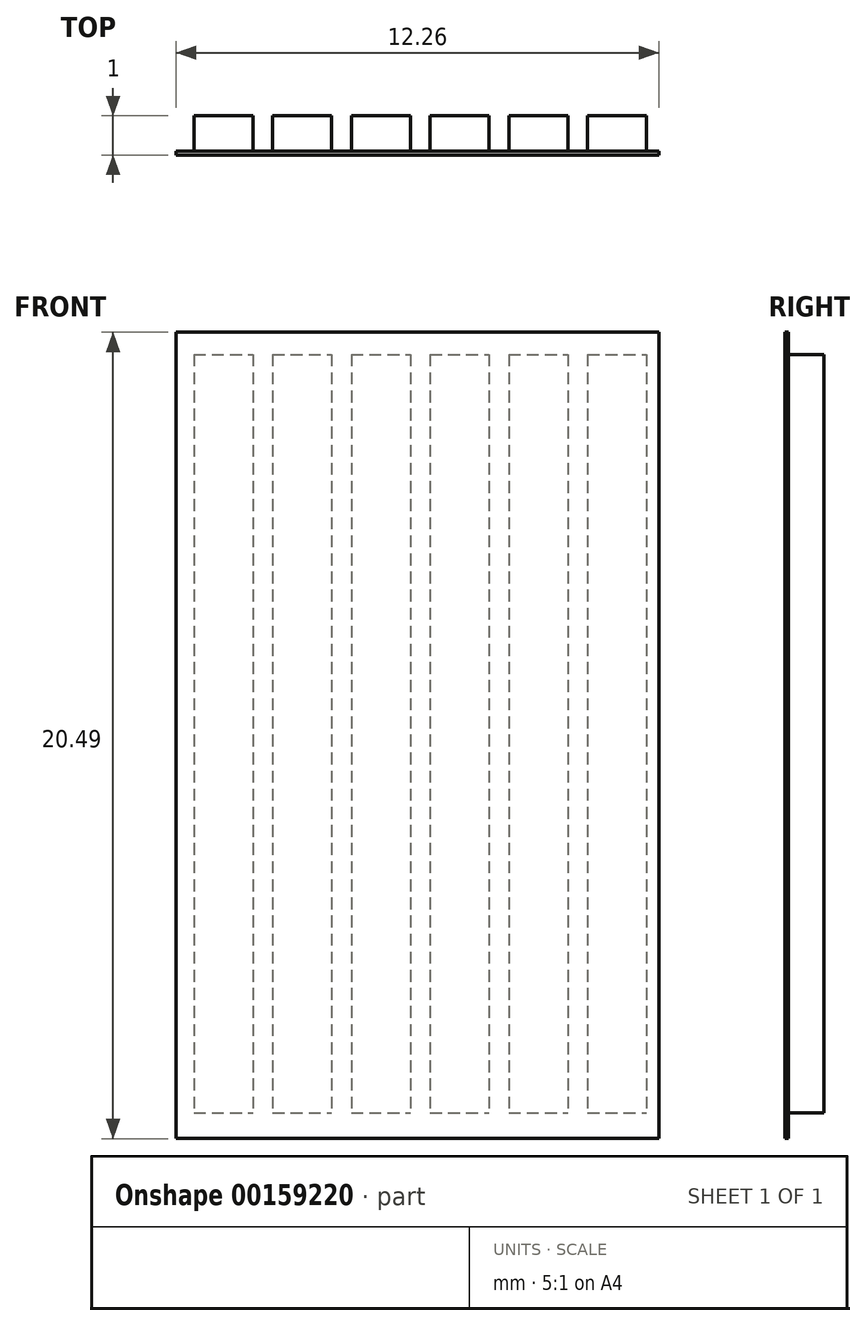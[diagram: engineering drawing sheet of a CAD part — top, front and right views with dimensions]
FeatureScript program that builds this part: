
annotation { "Feature Type Name" : "Feature", "Feature Type Description" : "" }
export const myFeature = defineFeature(function(context is Context, id is Id, definition is map)
    precondition{}
    {
        {
            var Q0;
            Q0=qCreatedBy(makeId("Front.planeOp"),FACE);
            var sketch = newSketch(context, id + "F0", { "sketchPlane" : qUnion([Q0])});
            skLineSegment(sketch, "E0.bottom", {"start": v(-57.17, 11.8) * mm, "end": v(-58.67, 11.8) * mm});
            skLineSegment(sketch, "E0.top", {"start": v(-57.17, 31.07) * mm, "end": v(-58.67, 31.07) * mm});
            skLineSegment(sketch, "E0.left", {"start": v(-57.17, 11.8) * mm, "end": v(-57.17, 31.07) * mm});
            skLineSegment(sketch, "E0.right", {"start": v(-58.67, 11.8) * mm, "end": v(-58.67, 31.07) * mm});
            skLineSegment(sketch, "E1.1.0.0", {"start": v(-56.67, 11.8) * mm, "end": v(-56.67, 31.07) * mm});
            skLineSegment(sketch, "E1.1.0.1", {"start": v(-55.17, 11.8) * mm, "end": v(-55.17, 31.07) * mm});
            skLineSegment(sketch, "E1.1.0.2", {"start": v(-55.17, 31.07) * mm, "end": v(-56.67, 31.07) * mm});
            skLineSegment(sketch, "E1.1.0.3", {"start": v(-55.17, 11.8) * mm, "end": v(-56.67, 11.8) * mm});
            skLineSegment(sketch, "E1.2.0.0", {"start": v(-54.67, 11.8) * mm, "end": v(-54.67, 31.07) * mm});
            skLineSegment(sketch, "E1.2.0.1", {"start": v(-53.17, 11.8) * mm, "end": v(-53.17, 31.07) * mm});
            skLineSegment(sketch, "E1.2.0.2", {"start": v(-53.17, 31.07) * mm, "end": v(-54.67, 31.07) * mm});
            skLineSegment(sketch, "E1.2.0.3", {"start": v(-53.17, 11.8) * mm, "end": v(-54.67, 11.8) * mm});
            skLineSegment(sketch, "E1.direction1", {"start": v(-58.67, 11.8) * mm, "end": v(-56.67, 11.8) * mm, "construction": true});
            skLineSegment(sketch, "E2.0.3.0", {"start": v(-52.67, 11.8) * mm, "end": v(-52.67, 31.07) * mm});
            skLineSegment(sketch, "E2.3.3.0", {"start": v(-51.17, 11.8) * mm, "end": v(-51.17, 31.07) * mm});
            skLineSegment(sketch, "E2.6.3.0", {"start": v(-51.17, 31.07) * mm, "end": v(-52.67, 31.07) * mm});
            skLineSegment(sketch, "E2.9.3.0", {"start": v(-51.17, 11.8) * mm, "end": v(-52.67, 11.8) * mm});
            skLineSegment(sketch, "E2.0.4.0", {"start": v(-50.67, 11.8) * mm, "end": v(-50.67, 31.07) * mm});
            skLineSegment(sketch, "E2.3.4.0", {"start": v(-49.17, 11.8) * mm, "end": v(-49.17, 31.07) * mm});
            skLineSegment(sketch, "E2.6.4.0", {"start": v(-49.17, 31.07) * mm, "end": v(-50.67, 31.07) * mm});
            skLineSegment(sketch, "E2.9.4.0", {"start": v(-49.17, 11.8) * mm, "end": v(-50.67, 11.8) * mm});
            skLineSegment(sketch, "E3.0.5.0", {"start": v(-48.67, 11.8) * mm, "end": v(-48.67, 31.07) * mm});
            skLineSegment(sketch, "E3.3.5.0", {"start": v(-47.17, 11.8) * mm, "end": v(-47.17, 31.07) * mm});
            skLineSegment(sketch, "E3.6.5.0", {"start": v(-47.17, 31.07) * mm, "end": v(-48.67, 31.07) * mm});
            skLineSegment(sketch, "E3.9.5.0", {"start": v(-47.17, 11.8) * mm, "end": v(-48.67, 11.8) * mm});
            skLineSegment(sketch, "E4", {"start": v(-58.67, 11.8) * mm, "end": v(-47.17, 11.8) * mm});
            skSolve(sketch);
        }
        {
            var Q0;
            Q0 = qSketchRegion(id + "F0", true);
            extrude(context, id + "F1", {"entities" : qUnion([Q0]), "oppositeDirection" : true, "depth" : 1 * mm});
        }
        {
            var Q0;
            Q0=qCreatedBy(makeId("Front.planeOp"),FACE);
            var sketch = newSketch(context, id + "F2", { "sketchPlane" : qUnion([Q0])});
            skLineSegment(sketch, "E5.bottom", {"start": v(-59.12, 31.63) * mm, "end": v(-46.86, 31.63) * mm});
            skLineSegment(sketch, "E5.top", {"start": v(-59.12, 11.14) * mm, "end": v(-46.86, 11.14) * mm});
            skLineSegment(sketch, "E5.left", {"start": v(-59.12, 31.63) * mm, "end": v(-59.12, 11.14) * mm});
            skLineSegment(sketch, "E5.right", {"start": v(-46.86, 31.63) * mm, "end": v(-46.86, 11.14) * mm});
            skSolve(sketch);
        }
        {
            var Q0;
            Q0 = qSketchRegion(id + "F2", true);
            extrude(context, id + "F3", {"entities" : qUnion([Q0]), "operationType" : NewBodyOperationType.ADD, "oppositeDirection" : true, "depth" : 0.1 * mm});
        }
    });
